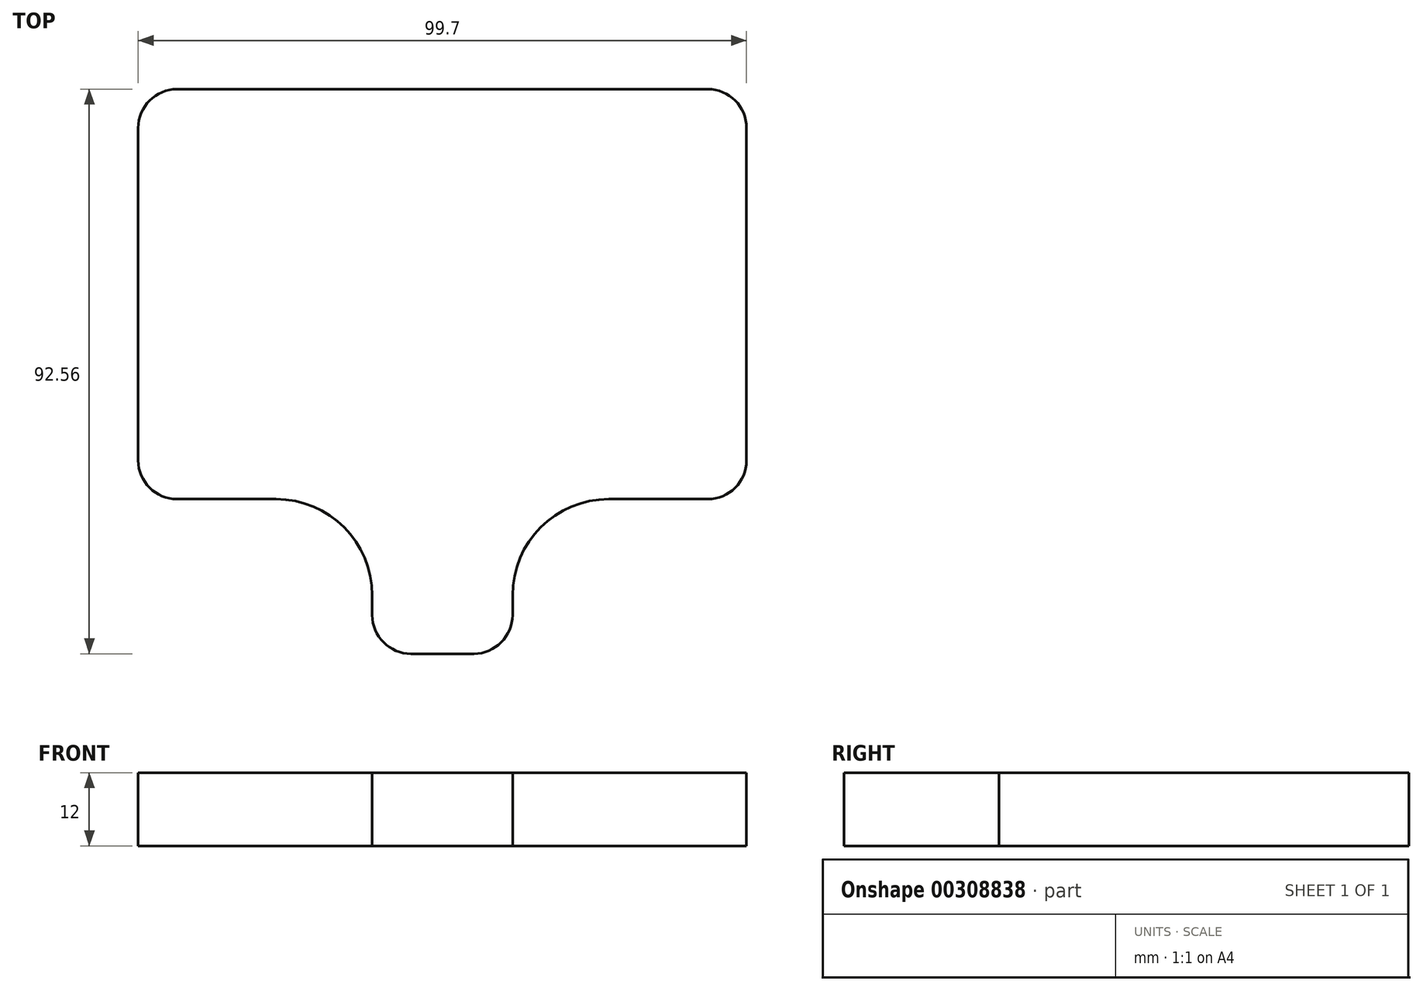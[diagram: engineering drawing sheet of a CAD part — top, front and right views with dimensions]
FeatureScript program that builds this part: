
annotation { "Feature Type Name" : "Feature", "Feature Type Description" : "" }
export const myFeature = defineFeature(function(context is Context, id is Id, definition is map)
    precondition{}
    {
        {
            var Q0;
            Q0=qCreatedBy(makeId("Top.planeOp"),FACE);
            var sketch = newSketch(context, id + "F0", { "sketchPlane" : qUnion([Q0])});
            skLineSegment(sketch, "E0.bottom", {"start": v(49.85, 46.28) * mm, "end": v(-49.85, 46.28) * mm});
            skLineSegment(sketch, "E0.top", {"start": v(11.5, -46.28) * mm, "end": v(-11.5, -46.28) * mm});
            skLineSegment(sketch, "E0.left", {"start": v(49.85, 46.28) * mm, "end": v(49.85, -20.94) * mm});
            skLineSegment(sketch, "E0.right", {"start": v(-49.85, 46.28) * mm, "end": v(-49.85, -20.94) * mm});
            skPoint(sketch, "E0.middle", {"position": v(0, 0) * mm});
            skArc(sketch, "E1", {"start": v(27.27, -20.94) * mm, "mid": v(16.12, -25.56) * mm, "end": v(11.5, -36.72) * mm});
            skArc(sketch, "E2.MirrorC", {"start": v(-27.27, -20.94) * mm, "mid": v(-16.12, -25.56) * mm, "end": v(-11.5, -36.72) * mm});
            skLineSegment(sketch, "E3", {"start": v(27.27, -20.94) * mm, "end": v(49.85, -20.94) * mm});
            skLineSegment(sketch, "E4", {"start": v(11.5, -36.72) * mm, "end": v(11.5, -46.28) * mm});
            skPoint(sketch, "E5.orphan", {"position": v(49.85, -46.28) * mm});
            skLineSegment(sketch, "E6.MirrorCS", {"start": v(-27.27, -20.94) * mm, "end": v(-49.85, -20.94) * mm});
            skLineSegment(sketch, "E7.MirrorCS", {"start": v(-11.5, -36.72) * mm, "end": v(-11.5, -46.28) * mm});
            skPoint(sketch, "E8.orphan", {"position": v(-49.85, -46.28) * mm});
            skSolve(sketch);
        }
        {
            var Q0;
            Q0 = qSketchRegion(id + "F0", true);
            extrude(context, id + "F1", {"entities" : qUnion([Q0]), "depth" : 12 * mm});
        }
        {
            var Q0;
            Q0=makeQuery(id+"F1.opExtrude","SWEPT_EDGE",EDGE,{"disambiguationData":[OSD([sQuery(id+"F0.wireOp",EDGE,"E0.bottom"),sQuery(id+"F0.wireOp",EDGE,"E0.right")])]});
            var Q1;
            Q1=makeQuery(id+"F1.opExtrude","SWEPT_EDGE",EDGE,{"disambiguationData":[OSD([sQuery(id+"F0.wireOp",EDGE,"E0.right"),sQuery(id+"F0.wireOp",EDGE,"E6.MirrorCS")])]});
            var Q2;
            Q2=makeQuery(id+"F1.opExtrude","SWEPT_EDGE",EDGE,{"disambiguationData":[OSD([sQuery(id+"F0.wireOp",EDGE,"E0.top"),sQuery(id+"F0.wireOp",EDGE,"E7.MirrorCS")])]});
            var Q3;
            Q3=makeQuery(id+"F1.opExtrude","SWEPT_EDGE",EDGE,{"disambiguationData":[OSD([sQuery(id+"F0.wireOp",EDGE,"E0.top"),sQuery(id+"F0.wireOp",EDGE,"E4")])]});
            var Q4;
            Q4=makeQuery(id+"F1.opExtrude","SWEPT_EDGE",EDGE,{"disambiguationData":[OSD([sQuery(id+"F0.wireOp",EDGE,"E0.left"),sQuery(id+"F0.wireOp",EDGE,"E3")])]});
            var Q5;
            Q5=makeQuery(id+"F1.opExtrude","SWEPT_EDGE",EDGE,{"disambiguationData":[OSD([sQuery(id+"F0.wireOp",EDGE,"E0.bottom"),sQuery(id+"F0.wireOp",EDGE,"E0.left")])]});
            fillet(context, id + "F2", {"entities" : qUnion([Q0, Q1, Q2, Q3, Q4, Q5]), "radius" : 6.35 * mm, "tangentPropagation" : true, "allowEdgeOverflow" : false});
        }
    });
